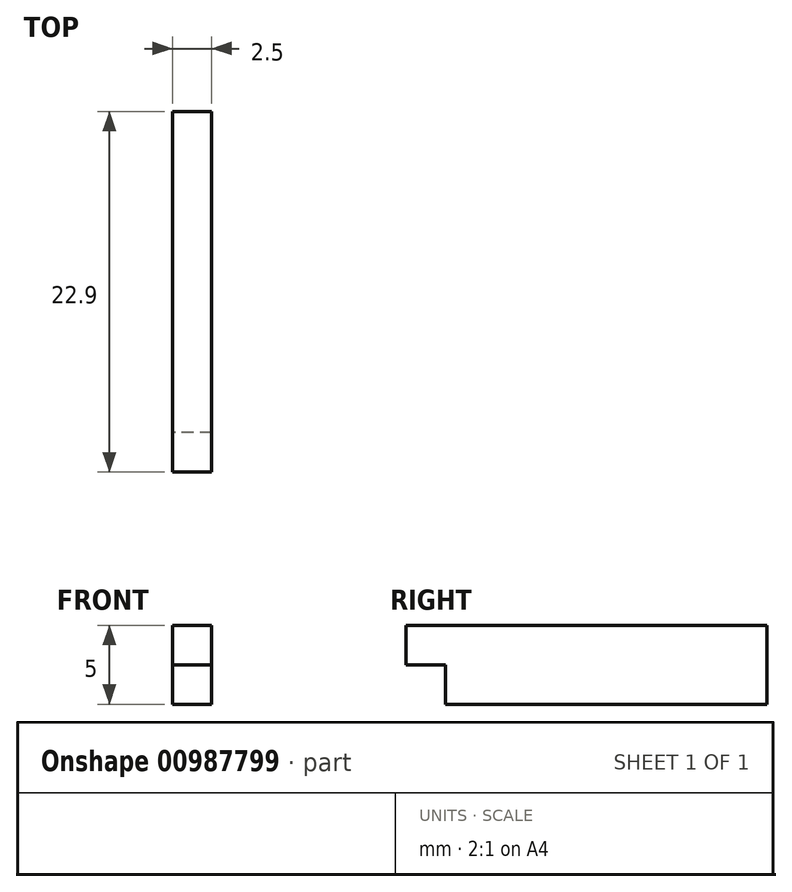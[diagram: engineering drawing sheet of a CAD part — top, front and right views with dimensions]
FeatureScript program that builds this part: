
annotation { "Feature Type Name" : "Feature", "Feature Type Description" : "" }
export const myFeature = defineFeature(function(context is Context, id is Id, definition is map)
    precondition{}
    {
        {
            var Q0;
            Q0=qCreatedBy(makeId("Right.planeOp"),FACE);
            var sketch = newSketch(context, id + "F0", { "sketchPlane" : qUnion([Q0])});
            skLineSegment(sketch, "E0", {"start": v(-2.2, 30.8) * mm, "end": v(-2.2, 28.3) * mm});
            skLineSegment(sketch, "E1", {"start": v(-2.2, 28.3) * mm, "end": v(0.3, 28.3) * mm});
            skLineSegment(sketch, "E2", {"start": v(0.3, 28.3) * mm, "end": v(0.3, 25.8) * mm});
            skLineSegment(sketch, "E3", {"start": v(0.3, 25.8) * mm, "end": v(20.7, 25.8) * mm});
            skLineSegment(sketch, "E4", {"start": v(20.7, 25.8) * mm, "end": v(20.7, 30.8) * mm});
            skLineSegment(sketch, "E5", {"start": v(20.7, 30.8) * mm, "end": v(-2.2, 30.8) * mm});
            skSolve(sketch);
        }
        {
            var Q0;
            Q0 = qSketchRegion(id + "F0", true);
            extrude(context, id + "F1", {"entities" : qUnion([Q0]), "depth" : 2.5 * mm, "offsetDistance" : 25 * mm});
        }
    });
